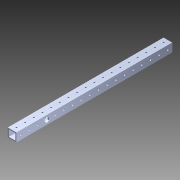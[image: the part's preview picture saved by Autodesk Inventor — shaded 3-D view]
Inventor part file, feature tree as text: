
AUTODESK INVENTOR PART (.ipt)
format: ipt  version: 2014 SP1 (Build 180222100, 222)  size: 1,279,488 bytes
history: native  units: in
note: dims shown in document units (in); Inventor stores cm internally (conversion verified against a paired STEP export)
features: sketch x3, extrude x2, pattern_circular x1, other x1, plane x1, imported_body x1
ambient origin geometry x8: Origin, YZ Plane, XZ Plane, XY Plane, X Axis, Y Axis, Z Axis, Center Point
bodies: Body1 (feature_tree)
feature tree (9):
  pattern_circular  "CirPattern2"
  other  "217-3426-STEP1"
  plane  "Work Plane1"
  extrude  "Extrusion1"  Depth=3937.0079in TaperAngle=0.0deg
  sketch  "Sketch3"  dims[d3=0.5in d5=2.0in d6=0.0in]
  extrude  "Extrusion2"  Depth=0.5in TaperAngle=0.0deg
  imported_body  "Base1"
  sketch  "Sketch1"  dims[d0=-18.0in d1=3937.0079in d2=0.0in]
  sketch  "Sketch4"
